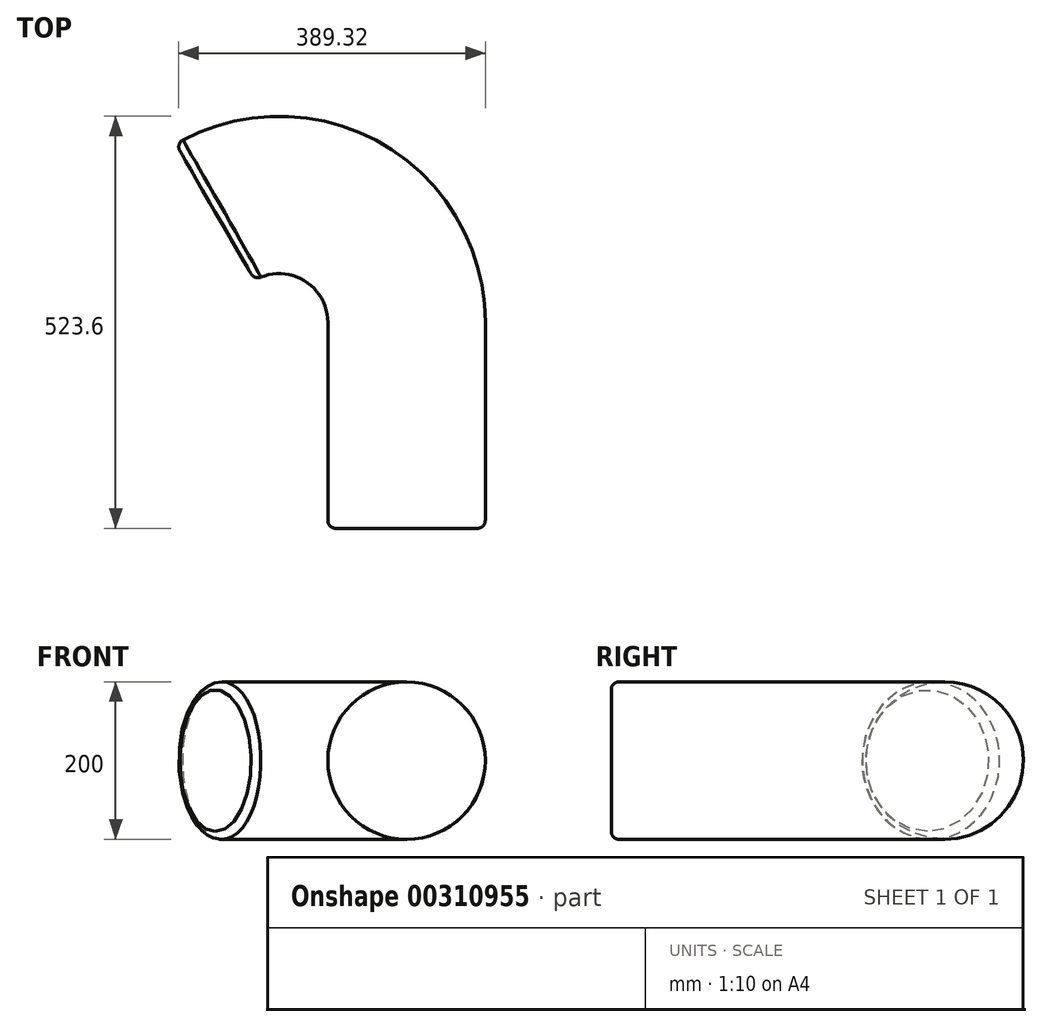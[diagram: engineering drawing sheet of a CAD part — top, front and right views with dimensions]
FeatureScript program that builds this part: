
annotation { "Feature Type Name" : "Feature", "Feature Type Description" : "" }
export const myFeature = defineFeature(function(context is Context, id is Id, definition is map)
    precondition{}
    {
        {
            var Q0;
            Q0=qCreatedBy(makeId("Top.planeOp"),FACE);
            var sketch = newSketch(context, id + "F0", { "sketchPlane" : qUnion([Q0])});
            skArc(sketch, "E0", {"start": v(161.8, 0) * mm, "mid": v(80.78, 140.2) * mm, "end": v(-81.14, 139.99) * mm});
            skLineSegment(sketch, "E1", {"start": v(161.8, 0) * mm, "end": v(161.8, -261.8) * mm});
            skSolve(sketch);
        }
        {
            var Q0;
            Q0=qCreatedBy(makeId("Front.planeOp"),FACE);
            var sketch = newSketch(context, id + "F1", { "sketchPlane" : qUnion([Q0])});
            skCircle(sketch, "E2", {"center": v(161.8, 0) * mm, "radius": 100 * mm});
            skSolve(sketch);
        }
        {
            var Q0;
            Q0=makeQuery(id+"F1.imprint","IMPRINT",FACE,{"disambiguationData":[TD([[makeQuery(id+"F1.imprint","IMPRINT",EDGE,{"derivedFrom":sQuery(id+"F1.wireOp",EDGE,"E2")}),1.0]])]});
            var Q1;
            Q1=sQuery(id+"F0.wireOp",EDGE,"E0");
            sweep(context, id + "F2", {"profiles" : qUnion([Q0]), "path" : qUnion([Q1])});
        }
        {
            var Q0;
            Q0=makeQuery(id+"F2.opSweep","CAP_FACE",FACE,{"disambiguationData":[OSD([sQuery(id+"F0.wireOp",VERTEX,"E0.start"),sQuery(id+"F1.wireOp",EDGE,"E2")])],"isStart":true});
            var Q1;
            Q1=sQuery(id+"F0.wireOp",EDGE,"E1");
            sweep(context, id + "F3", {"operationType" : NewBodyOperationType.ADD, "profiles" : qUnion([Q0]), "path" : qUnion([Q1])});
        }
        {
            var Q0;
            Q0=makeQuery(id+"F3.opSweep","CAP_FACE",FACE,{"disambiguationData":[OSD([sQuery(id+"F0.wireOp",VERTEX,"E0.start"),sQuery(id+"F0.wireOp",VERTEX,"E1.end"),sQuery(id+"F1.wireOp",EDGE,"E2")])],"isStart":false});
            var sketch = newSketch(context, id + "F4", { "sketchPlane" : qUnion([Q0])});
            skCircle(sketch, "E3", {"center": v(161.8, 0) * mm, "radius": 158.54 * mm});
            skCircle(sketch, "E4", {"center": v(161.8, 0) * mm, "radius": 100 * mm});
            skSolve(sketch);
        }
        {
            var Q0;
            Q0=makeQuery(id+"F4.imprint","IMPRINT",FACE,{"disambiguationData":[TD([[makeQuery(id+"F4.imprint","IMPRINT",EDGE,{"derivedFrom":sQuery(id+"F4.wireOp",EDGE,"E3")}),1.0]])]});
            extrude(context, id + "F5", {"entities" : qUnion([Q0]), "operationType" : NewBodyOperationType.REMOVE, "depth" : -261 * mm});
        }
        {
            var Q0;
            Q0=makeQuery(id+"F3.opSweep","CAP_EDGE",EDGE,{"disambiguationData":[OSD([sQuery(id+"F0.wireOp",VERTEX,"E0.start"),sQuery(id+"F0.wireOp",VERTEX,"E1.end"),sQuery(id+"F1.wireOp",EDGE,"E2")])],"isStart":false});
            var Q1;
            Q1=makeQuery(id+"F5.boolean.opBoolean","MERGE",FACE,{"derivedFrom":[makeQuery(id+"F3.opSweep","SWEPT_FACE",FACE,{"disambiguationData":[OSD([sQuery(id+"F0.wireOp",VERTEX,"E0.start"),sQuery(id+"F0.wireOp",EDGE,"E1"),sQuery(id+"F1.wireOp",EDGE,"E2")])]}),makeQuery(id+"F5.opExtrude","SWEPT_FACE",FACE,{"disambiguationData":[OSD([sQuery(id+"F4.wireOp",EDGE,"E4")])]})]});
            fillet(context, id + "F6", {"entities" : qUnion([Q0, Q1]), "radius" : 10 * mm, "tangentPropagation" : true, "allowEdgeOverflow" : false});
        }
        {
            var Q0;
            Q0=makeQuery(id+"F2.opSweep","CAP_EDGE",EDGE,{"disambiguationData":[OSD([sQuery(id+"F0.wireOp",VERTEX,"E0.end"),sQuery(id+"F1.wireOp",EDGE,"E2")])],"isStart":false});
            fillet(context, id + "F7", {"entities" : qUnion([Q0]), "radius" : 10 * mm, "tangentPropagation" : true, "allowEdgeOverflow" : false});
        }
    });
